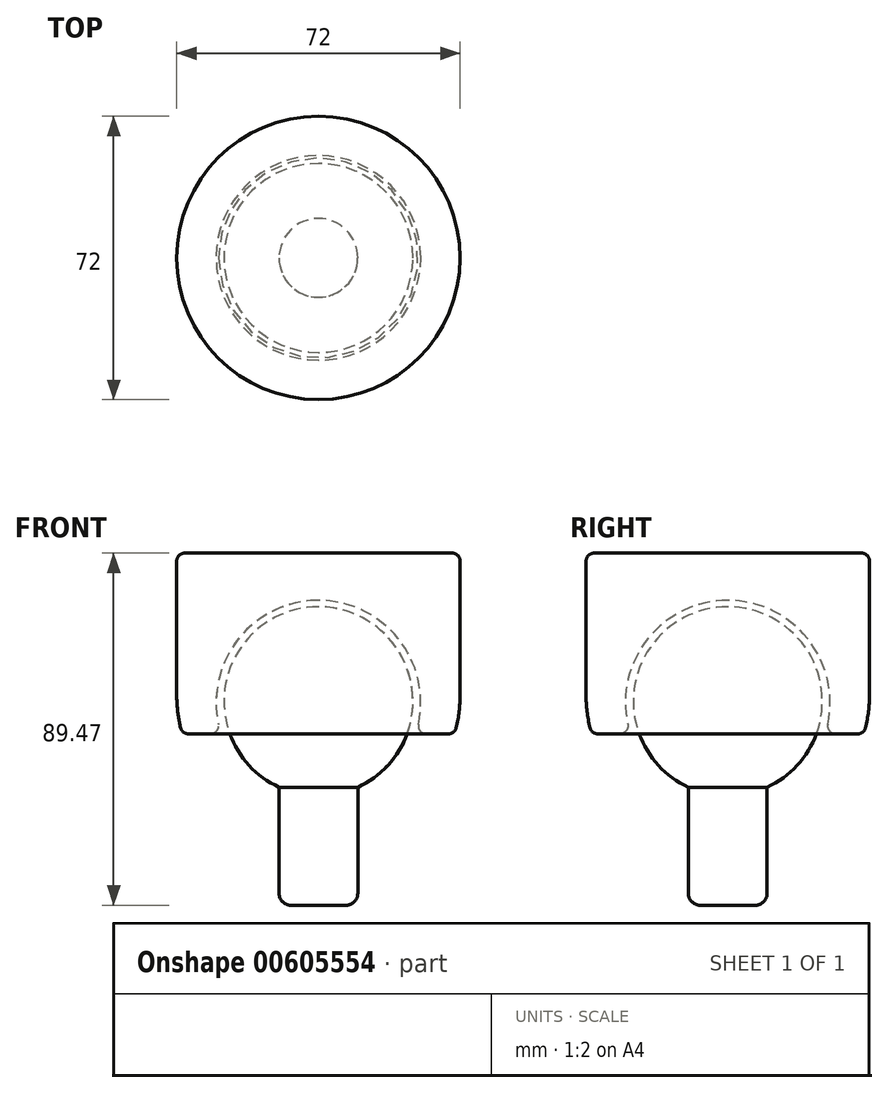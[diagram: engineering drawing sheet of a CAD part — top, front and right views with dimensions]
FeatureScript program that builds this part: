
annotation { "Feature Type Name" : "Feature", "Feature Type Description" : "" }
export const myFeature = defineFeature(function(context is Context, id is Id, definition is map)
    precondition{}
    {
        {
            var Q0;
            Q0=qCreatedBy(makeId("Front.planeOp"),FACE);
            var sketch = newSketch(context, id + "F0", { "sketchPlane" : qUnion([Q0])});
            skLineSegment(sketch, "E0", {"start": v(-10, 0) * mm, "end": v(0, 0) * mm});
            skArc(sketch, "E1", {"start": v(0, 75.82) * mm, "mid": v(-23.45, 56.94) * mm, "end": v(-10, 30) * mm});
            skLineSegment(sketch, "E2", {"start": v(-10, 30) * mm, "end": v(-10, 0) * mm});
            skLineSegment(sketch, "E3", {"start": v(0, 75.82) * mm, "end": v(0, 0) * mm});
            skPoint(sketch, "E4.end.orphan", {"position": v(10, 30) * mm});
            skSolve(sketch);
        }
        {
            var Q0;
            {var subQ0=sQuery(id+"F0.wireOp",EDGE,"E2");Q0=makeQuery(id+"F0.imprint","IMPRINT",FACE,{"disambiguationData":[TD([[makeQuery(id+"F0.imprint","IMPRINT",EDGE,{"derivedFrom":subQ0}),1.0]])]});}
            var Q1;
            Q1=sQuery(id+"F0.wireOp",EDGE,"E3");
            revolve(context, id + "F1", {"entities" : qUnion([Q0]), "axis" : qUnion([Q1]), "revolveType" : RevolveType.FULL});
        }
        {
            var Q0;
            Q0=makeQuery(id+"F1.opRevolve","SWEPT_FACE",FACE,{"disambiguationData":[OSD([sQuery(id+"F0.wireOp",EDGE,"E0")])]});
            fillet(context, id + "F2", {"entities" : qUnion([Q0]), "radius" : 3 * mm, "tangentPropagation" : true, "allowEdgeOverflow" : false});
        }
        {
            var Q0;
            Q0=qCreatedBy(makeId("Front.planeOp"),FACE);
            var sketch = newSketch(context, id + "F3", { "sketchPlane" : qUnion([Q0])});
            skLineSegment(sketch, "E5", {"start": v(0, 51.47) * mm, "end": v(0, 53.47) * mm, "construction": true});
            skArc(sketch, "E6", {"start": v(0, 77.47) * mm, "mid": v(-24.96, 58.76) * mm, "end": v(-14, 29.56) * mm});
            skArc(sketch, "E7", {"start": v(-36, 53.47) * mm, "mid": v(-33.65, 40.68) * mm, "end": v(-26.91, 29.56) * mm});
            skLineSegment(sketch, "E8", {"start": v(0, 89.47) * mm, "end": v(-36, 89.47) * mm});
            skLineSegment(sketch, "E9", {"start": v(-36, 89.47) * mm, "end": v(-36, 53.47) * mm});
            skPoint(sketch, "E10.start.orphan", {"position": v(-41.87, 150.12) * mm});
            skPoint(sketch, "E11.orphan", {"position": v(-49.11, 66.47) * mm});
            skPoint(sketch, "E12.orphan", {"position": v(-8, 66.47) * mm});
            skPoint(sketch, "E13.start.orphan", {"position": v(33.13, 66.47) * mm});
            skPoint(sketch, "E14.orphan", {"position": v(-49.11, 27.43) * mm});
            skLineSegment(sketch, "E15", {"start": v(-14, 29.56) * mm, "end": v(0, 29.56) * mm, "construction": true});
            skLineSegment(sketch, "E16", {"start": v(0, 29.56) * mm, "end": v(0, 89.47) * mm});
            skLineSegment(sketch, "E17", {"start": v(-14, 29.56) * mm, "end": v(-26.91, 29.56) * mm, "construction": true});
            skLineSegment(sketch, "E18", {"start": v(-26.91, 29.56) * mm, "end": v(-26.91, 43.56) * mm, "construction": true});
            skLineSegment(sketch, "E19", {"start": v(-26.91, 43.56) * mm, "end": v(-24.77, 43.56) * mm});
            skLineSegment(sketch, "E20", {"start": v(-26.91, 43.56) * mm, "end": v(-34.6, 43.56) * mm});
            skSolve(sketch);
        }
        {
            var Q0;
            {var subQ1=sQuery(id+"F3.wireOp",EDGE,"E6");Q0=makeQuery(id+"F3.imprint","IMPRINT",FACE,{"disambiguationData":[TD([[makeQuery(id+"F3.imprint","IMPRINT",EDGE,{"derivedFrom":subQ1}),-1.0]])]});}
            var Q1;
            Q1=sQuery(id+"F3.wireOp",EDGE,"E16");
            revolve(context, id + "F4", {"surfaceOperationType" : NewSurfaceOperationType.NEW, "entities" : qUnion([Q0]), "axis" : qUnion([Q1]), "revolveType" : RevolveType.FULL});
        }
        {
            var Q0;
            Q0=makeQuery(id+"F4.opRevolve","SWEPT_FACE",FACE,{"disambiguationData":[OSD([sQuery(id+"F3.wireOp",EDGE,"E7")])]});
            var Q1;
            Q1=makeQuery(id+"F4.opRevolve","SWEPT_EDGE",EDGE,{"disambiguationData":[OSD([sQuery(id+"F3.wireOp",EDGE,"E7"),sQuery(id+"F3.wireOp",EDGE,"E9")])]});
            var Q2;
            Q2=makeQuery(id+"F4.opRevolve","SWEPT_EDGE",EDGE,{"disambiguationData":[OSD([sQuery(id+"F3.wireOp",EDGE,"E8"),sQuery(id+"F3.wireOp",EDGE,"E9")])]});
            fillet(context, id + "F5", {"entities" : qUnion([Q0, Q1, Q2]), "radius" : 2 * mm, "tangentPropagation" : true, "allowEdgeOverflow" : false});
        }
        {
            var Q0;
            Q0=makeQuery(id+"F4.opRevolve","SWEPT_EDGE",EDGE,{"disambiguationData":[OSD([sQuery(id+"F3.wireOp",EDGE,"E6"),sQuery(id+"F3.wireOp",EDGE,"S6m84c3j-o0aE-6wpa-2qxI-uG5NYIwbioCe")])]});
            fillet(context, id + "F6", {"entities" : qUnion([Q0]), "radius" : 2 * mm, "tangentPropagation" : true, "allowEdgeOverflow" : false});
        }
    });
